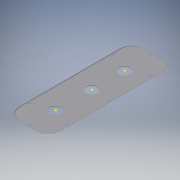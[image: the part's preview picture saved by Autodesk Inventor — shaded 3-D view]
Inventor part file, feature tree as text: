
AUTODESK INVENTOR PART (.ipt)
format: ipt  version: 2017 (Build 210142000, 142)  size: 158,208 bytes
history: native  units: in
note: dims shown in document units (in); Inventor stores cm internally (conversion verified against a paired STEP export)
features: hole x3, sketch x3, other x1
ambient origin geometry x8: Origin, YZ Plane, XZ Plane, XY Plane, X Axis, Y Axis, Z Axis, Center Point
bodies: Solid1 (feature_tree)
feature tree (7):
  other  "nsycrn106250t"
  hole  "Hole1"  [1 undecoded]
  hole  "Hole2"  [1 undecoded]
  hole  "Hole3"  [1 undecoded]
  sketch  "Sketch1"  dims[d0=0.3937in d1=0.3937in]
  sketch  "Sketch2"  dims[d2=1.5748in d3=0.2362in d4=0.1575in d5=0.0787in d6=90.0deg d7=0.315in d8=0.8108in d9=0.3937in d10=0.3937in]
  sketch  "Sketch3"  dims[d11=1.5748in d12=0.2362in d13=0.1575in d14=0.0787in d15=90.0deg d16=0.315in d17=0.8108in d18=0.3937in d19=0.3937in d20=1.5748in d21=0.2362in d22=0.1575in d23=0.0787in d24=90.0deg d25=0.315in d26=0.8108in]
note: 3 required parameter values undecoded (feature->parameter linkage not recoverable at this tier; creation-order binding heuristic only, values carry confidence <= 0.55)
